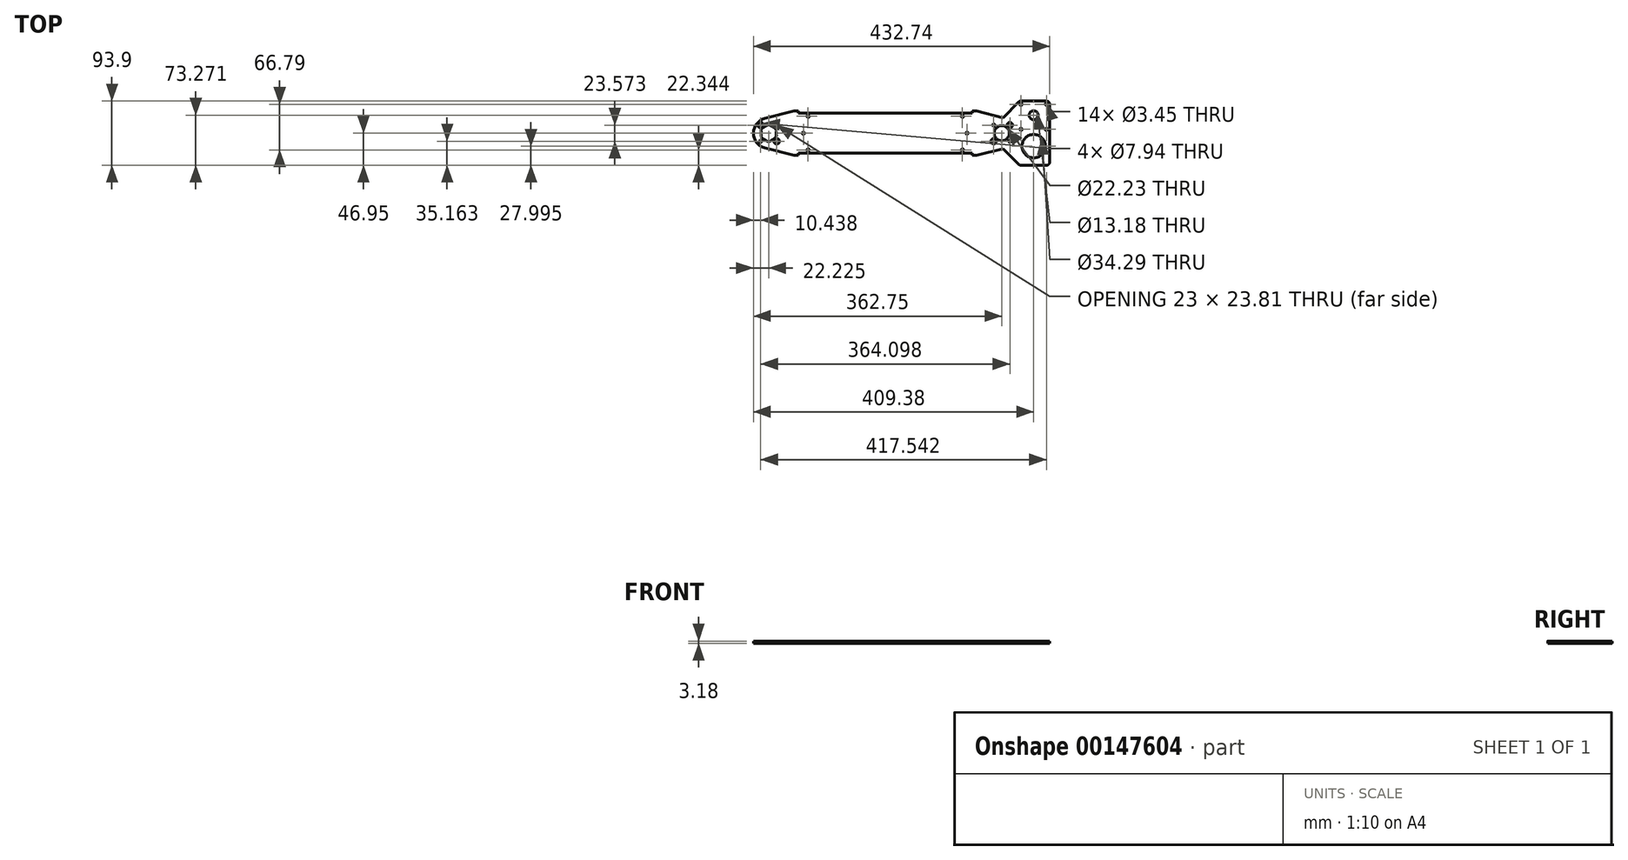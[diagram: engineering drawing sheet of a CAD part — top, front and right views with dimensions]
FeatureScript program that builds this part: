
annotation { "Feature Type Name" : "Feature", "Feature Type Description" : "" }
export const myFeature = defineFeature(function(context is Context, id is Id, definition is map)
    precondition{}
    {
        {
            var Q0;
            Q0=qCreatedBy(makeId("Top.planeOp"),FACE);
            var sketch = newSketch(context, id + "F0", { "sketchPlane" : qUnion([Q0])});
            skPoint(sketch, "E0.rect.middle", {"position": v(0, 0) * mm});
            skCircle(sketch, "E1", {"center": v(0, 0) * mm, "radius": 11.11 * mm});
            skLineSegment(sketch, "E2.bottom", {"start": v(11.79, 11.79) * mm, "end": v(-11.79, 11.79) * mm, "construction": true});
            skLineSegment(sketch, "E2.left", {"start": v(11.79, 11.79) * mm, "end": v(11.79, -11.79) * mm, "construction": true});
            skLineSegment(sketch, "E2.right", {"start": v(-11.79, 11.79) * mm, "end": v(-11.79, -11.79) * mm, "construction": true});
            skCircle(sketch, "E3", {"center": v(-11.79, 11.79) * mm, "radius": 1.73 * mm});
            skCircle(sketch, "E4", {"center": v(11.79, 11.79) * mm, "radius": 3.97 * mm});
            skCircle(sketch, "E5", {"center": v(11.79, -11.79) * mm, "radius": 1.73 * mm});
            skCircle(sketch, "E6", {"center": v(-11.79, -11.79) * mm, "radius": 3.97 * mm});
            skArc(sketch, "E7", {"start": v(-346.1, 21.51) * mm, "mid": v(-362.75, 0) * mm, "end": v(-346.1, -21.51) * mm});
            skLineSegment(sketch, "E8.bottom", {"start": v(-352.31, 11.79) * mm, "end": v(-328.74, 11.79) * mm, "construction": true});
            skLineSegment(sketch, "E8.top", {"start": v(-352.31, -11.79) * mm, "end": v(-328.74, -11.79) * mm, "construction": true});
            skLineSegment(sketch, "E8.left", {"start": v(-352.31, 11.79) * mm, "end": v(-352.31, -11.79) * mm, "construction": true});
            skLineSegment(sketch, "E8.right", {"start": v(-328.74, 11.79) * mm, "end": v(-328.74, -11.79) * mm, "construction": true});
            skCircle(sketch, "E9", {"center": v(-328.74, 11.79) * mm, "radius": 1.73 * mm});
            skCircle(sketch, "E10", {"center": v(-340.53, 0) * mm, "radius": 11.11 * mm});
            skCircle(sketch, "E11", {"center": v(-352.31, 11.79) * mm, "radius": 3.97 * mm});
            skCircle(sketch, "E12", {"center": v(-352.31, -11.79) * mm, "radius": 1.73 * mm});
            skCircle(sketch, "E13", {"center": v(-328.74, -11.79) * mm, "radius": 3.97 * mm});
            skLineSegment(sketch, "E14", {"start": v(0, 0) * mm, "end": v(-340.53, 0) * mm, "construction": true});
            skLineSegment(sketch, "E15", {"start": v(-346.1, -21.51) * mm, "end": v(-303.61, -32.54) * mm});
            skLineSegment(sketch, "E16", {"start": v(-346.1, 21.51) * mm, "end": v(-303.61, 32.54) * mm});
            skLineSegment(sketch, "E17", {"start": v(-297.26, -29.37) * mm, "end": v(-43.26, -29.37) * mm});
            skLineSegment(sketch, "E18", {"start": v(-297.26, 29.37) * mm, "end": v(-43.26, 29.37) * mm});
            skLineSegment(sketch, "E19", {"start": v(-297.26, 32.54) * mm, "end": v(-297.26, 29.37) * mm});
            skLineSegment(sketch, "E20", {"start": v(-297.26, 32.54) * mm, "end": v(-303.61, 32.54) * mm});
            skLineSegment(sketch, "E21", {"start": v(-297.26, -29.37) * mm, "end": v(-297.26, -32.54) * mm});
            skLineSegment(sketch, "E22", {"start": v(-297.26, -32.54) * mm, "end": v(-303.61, -32.54) * mm});
            skLineSegment(sketch, "E23", {"start": v(-43.26, -29.37) * mm, "end": v(-43.26, -32.54) * mm});
            skLineSegment(sketch, "E24", {"start": v(-43.26, -32.54) * mm, "end": v(-36.91, -32.54) * mm});
            skLineSegment(sketch, "E25", {"start": v(-43.26, 29.37) * mm, "end": v(-43.26, 32.54) * mm});
            skLineSegment(sketch, "E26", {"start": v(-43.26, 32.54) * mm, "end": v(-36.91, 32.54) * mm});
            skLineSegment(sketch, "E27", {"start": v(-36.91, -32.54) * mm, "end": v(1.65, -22.53) * mm});
            skLineSegment(sketch, "E28", {"start": v(1.65, 22.53) * mm, "end": v(-36.91, 32.54) * mm});
            skLineSegment(sketch, "E29", {"start": v(-297.26, 29.37) * mm, "end": v(-297.26, 24.6) * mm, "construction": true});
            skLineSegment(sketch, "E30", {"start": v(-297.26, 24.6) * mm, "end": v(-282.98, 24.6) * mm, "construction": true});
            skLineSegment(sketch, "E31", {"start": v(-297.26, -29.37) * mm, "end": v(-297.26, -24.6) * mm, "construction": true});
            skLineSegment(sketch, "E32", {"start": v(-297.26, -24.6) * mm, "end": v(-282.98, -24.6) * mm, "construction": true});
            skLineSegment(sketch, "E33", {"start": v(-43.26, -29.37) * mm, "end": v(-43.26, -24.6) * mm, "construction": true});
            skLineSegment(sketch, "E34", {"start": v(-43.26, -24.6) * mm, "end": v(-57.55, -24.6) * mm, "construction": true});
            skLineSegment(sketch, "E35", {"start": v(-43.26, 29.37) * mm, "end": v(-43.26, 24.6) * mm, "construction": true});
            skLineSegment(sketch, "E36", {"start": v(-43.26, 24.6) * mm, "end": v(-57.55, 24.6) * mm, "construction": true});
            skCircle(sketch, "E37", {"center": v(-282.98, 24.6) * mm, "radius": 1.73 * mm});
            skCircle(sketch, "E38", {"center": v(-57.55, 24.6) * mm, "radius": 1.73 * mm});
            skCircle(sketch, "E39", {"center": v(-57.55, -24.6) * mm, "radius": 1.73 * mm});
            skCircle(sketch, "E40", {"center": v(-282.98, -24.6) * mm, "radius": 1.73 * mm});
            skLineSegment(sketch, "E41", {"start": v(-11.79, -11.79) * mm, "end": v(11.79, -11.79) * mm, "construction": true});
            skLineSegment(sketch, "E42", {"start": v(-170.26, -29.37) * mm, "end": v(-170.26, 0) * mm, "construction": true});
            skLineSegment(sketch, "E43", {"start": v(-170.26, 0) * mm, "end": v(-170.26, 29.37) * mm, "construction": true});
            skLineSegment(sketch, "E44", {"start": v(-328.74, 11.79) * mm, "end": v(-289.73, 11.79) * mm, "construction": true});
            skLineSegment(sketch, "E45", {"start": v(-289.73, 11.79) * mm, "end": v(-289.73, 0) * mm, "construction": true});
            skLineSegment(sketch, "E46", {"start": v(-11.79, 11.79) * mm, "end": v(-50.8, 11.79) * mm, "construction": true});
            skLineSegment(sketch, "E47", {"start": v(-50.8, 11.79) * mm, "end": v(-50.8, 0) * mm, "construction": true});
            skCircle(sketch, "E48", {"center": v(-289.73, 0) * mm, "radius": 1.73 * mm});
            skCircle(sketch, "E49", {"center": v(-50.8, 0) * mm, "radius": 1.73 * mm});
            skLineSegment(sketch, "E50", {"start": v(1.65, 22.53) * mm, "end": v(5.58, 21.51) * mm, "construction": true});
            skLineSegment(sketch, "E51", {"start": v(1.65, -22.53) * mm, "end": v(5.58, -21.51) * mm, "construction": true});
            skLineSegment(sketch, "E52", {"start": v(0, 0) * mm, "end": v(46.63, 0) * mm, "construction": true});
            skLineSegment(sketch, "E53", {"start": v(46.63, 11.59) * mm, "end": v(46.63, -11.59) * mm, "construction": true});
            skLineSegment(sketch, "E54", {"start": v(46.63, 0) * mm, "end": v(70, 0) * mm, "construction": true});
            skLineSegment(sketch, "E55", {"start": v(1.65, 22.53) * mm, "end": v(24.66, 45.55) * mm});
            skLineSegment(sketch, "E56", {"start": v(1.65, -22.53) * mm, "end": v(24.66, -45.55) * mm});
            skArc(sketch, "E57", {"start": v(5.58, -21.51) * mm, "mid": v(22.23, 0) * mm, "end": v(5.58, 21.51) * mm, "construction": true});
            skLineSegment(sketch, "E58", {"start": v(46.63, 11.59) * mm, "end": v(46.63, 26.32) * mm, "construction": true});
            skLineSegment(sketch, "E59", {"start": v(46.63, -11.59) * mm, "end": v(46.63, -26.32) * mm, "construction": true});
            skCircle(sketch, "E60", {"center": v(46.63, 18.95) * mm, "radius": 18.16 * mm, "construction": true});
            skCircle(sketch, "E61", {"center": v(28.03, 42.18) * mm, "radius": 1.73 * mm});
            skCircle(sketch, "E62", {"center": v(65.23, 5.56) * mm, "radius": 1.73 * mm});
            skCircle(sketch, "E63", {"center": v(28.03, 5.56) * mm, "radius": 1.73 * mm});
            skArc(sketch, "E64", {"start": v(28.03, 46.95) * mm, "mid": v(26.2, 46.58) * mm, "end": v(24.66, 45.55) * mm});
            skLineSegment(sketch, "E65", {"start": v(28.03, 46.95) * mm, "end": v(70, 46.95) * mm});
            skLineSegment(sketch, "E66", {"start": v(70, 46.95) * mm, "end": v(70, -46.95) * mm});
            skLineSegment(sketch, "E67", {"start": v(70, -46.95) * mm, "end": v(28.03, -46.95) * mm});
            skArc(sketch, "E68", {"start": v(24.66, -45.55) * mm, "mid": v(26.2, -46.58) * mm, "end": v(28.03, -46.95) * mm});
            skLineSegment(sketch, "E69", {"start": v(46.63, 26.32) * mm, "end": v(46.63, 46.95) * mm, "construction": true});
            skLineSegment(sketch, "E70.bottom", {"start": v(28.03, 42.18) * mm, "end": v(65.23, 42.18) * mm, "construction": true});
            skLineSegment(sketch, "E70.top", {"start": v(28.03, 5.56) * mm, "end": v(65.23, 5.56) * mm, "construction": true});
            skLineSegment(sketch, "E70.left", {"start": v(28.03, 42.18) * mm, "end": v(28.03, 5.56) * mm, "construction": true});
            skLineSegment(sketch, "E70.right", {"start": v(65.23, 42.18) * mm, "end": v(65.23, 5.56) * mm, "construction": true});
            skArc(sketch, "E71", {"start": v(65.23, 0.8) * mm, "mid": v(68.6, 2.19) * mm, "end": v(70, 5.56) * mm, "construction": true});
            skLineSegment(sketch, "E72", {"start": v(65.23, 0.8) * mm, "end": v(46.63, 0.8) * mm, "construction": true});
            skArc(sketch, "E73", {"start": v(70, 5.56) * mm, "mid": v(61.86, 8.92) * mm, "end": v(65.23, 0.8) * mm, "construction": true});
            skPoint(sketch, "E74", {"position": v(46.63, 42.18) * mm});
            skCircle(sketch, "E75", {"center": v(46.63, 26.32) * mm, "radius": 6.59 * mm});
            skCircle(sketch, "E76", {"center": v(65.23, 42.18) * mm, "radius": 1.73 * mm});
            skCircle(sketch, "E77", {"center": v(46.63, -18.95) * mm, "radius": 17.15 * mm});
            skCircle(sketch, "E78", {"center": v(28.03, 5.56) * mm, "radius": 6.35 * mm, "construction": true});
            skSolve(sketch);
        }
        {
            var Q0;
            Q0=qSketchRegion(id+"F0",true);
            extrude(context, id + "F1", {"entities" : qUnion([Q0]), "depth" : 3.17 * mm});
        }
        {
            var Q0;
            Q0=makeQuery(id+"F1.opExtrude","CAP_FACE",FACE,{"disambiguationData":[OSD([sQuery(id+"F0.wireOp",EDGE,"d63eafa0-1946-4b0e-8293-95e246b273c5.rect.bottom"),sQuery(id+"F0.wireOp",EDGE,"d63eafa0-1946-4b0e-8293-95e246b273c5.rect.top"),sQuery(id+"F0.wireOp",EDGE,"5983dcdd-59a7-4b72-80fd-e4567be1ae8a"),sQuery(id+"F0.wireOp",EDGE,"5a538b3e-fc2b-4d64-affd-5d60433388e5"),sQuery(id+"F0.wireOp",EDGE,"72e86de7-b207-474f-aadf-64543fae3f9b"),sQuery(id+"F0.wireOp",EDGE,"1c038800-5bd5-4753-8b38-6da13ef78ef9"),sQuery(id+"F0.wireOp",EDGE,"EbMUZoU6-Ffds-1dNq-SxhE-hPi8oSjhvaod"),sQuery(id+"F0.wireOp",EDGE,"RfgQjzcw-1Izs-lnTa-bWkk-oBHRDQjbZqQC"),sQuery(id+"F0.wireOp",EDGE,"1cCQAcjj-TyQA-3DMx-kDix-v5yZVaaGeXVM"),sQuery(id+"F0.wireOp",EDGE,"7KPu8lni-3ZWA-t6oJ-FRoh-C5MB3aVr7E9B"),sQuery(id+"F0.wireOp",EDGE,"bSzr06ES-7M0i-Fw5H-UJmt-4e4EQGRPIe4n"),sQuery(id+"F0.wireOp",EDGE,"WGsr6OjU-OX8l-mawA-7cCc-MfOuMOY06Cp5"),sQuery(id+"F0.wireOp",EDGE,"9mrz1cDN-18gM-20ra-6VCO-jp25g10tvNn2"),sQuery(id+"F0.wireOp",EDGE,"G0uOisy3-Mq6h-PcKh-Zkf4-CVoCvP3Hii1l"),sQuery(id+"F0.wireOp",EDGE,"1ae556be-0ab9-4322-b48e-98cf5a741ae0"),sQuery(id+"F0.wireOp",EDGE,"676cd913-43f8-42b3-8cdc-a90136d19ef5"),sQuery(id+"F0.wireOp",EDGE,"xnt2EyF8-ZVyQ-RbWD-GIsP-ThkcyX8ZioIH.bottom"),sQuery(id+"F0.wireOp",EDGE,"xnt2EyF8-ZVyQ-RbWD-GIsP-ThkcyX8ZioIH.top"),sQuery(id+"F0.wireOp",EDGE,"xnt2EyF8-ZVyQ-RbWD-GIsP-ThkcyX8ZioIH.left"),sQuery(id+"F0.wireOp",EDGE,"E1"),sQuery(id+"F0.wireOp",EDGE,"Jo9pZc7T-t0kF-vjz1-dNbX-L65bwNqtrrdz"),sQuery(id+"F0.wireOp",EDGE,"lEYoY9t7-PMOS-SVp6-xfnB-Xp9WdWMCDdum"),sQuery(id+"F0.wireOp",EDGE,"s7aM02SC-9XQ7-dueL-DqMg-ZFuJqOofj9mt"),sQuery(id+"F0.wireOp",EDGE,"deKa9ngt-XMq2-GGkr-SZIa-KlyN0U5bcCDe"),sQuery(id+"F0.wireOp",EDGE,"E3"),sQuery(id+"F0.wireOp",EDGE,"E4"),sQuery(id+"F0.wireOp",EDGE,"E5"),sQuery(id+"F0.wireOp",EDGE,"E6"),sQuery(id+"F0.wireOp",EDGE,"E7"),sQuery(id+"F0.wireOp",EDGE,"E9"),sQuery(id+"F0.wireOp",EDGE,"E10"),sQuery(id+"F0.wireOp",EDGE,"E11"),sQuery(id+"F0.wireOp",EDGE,"E12"),sQuery(id+"F0.wireOp",EDGE,"E13")])],"isStart":true});
            var sketch = newSketch(context, id + "F2", { "sketchPlane" : qUnion([Q0])});
            skLineSegment(sketch, "E79", {"start": v(-340.53, 0) * mm, "end": v(-350.15, -5.56) * mm, "construction": true});
            skArc(sketch, "E80", {"start": v(-351.26, -2.88) * mm, "mid": v(-350.15, -5.56) * mm, "end": v(-348.38, -7.86) * mm});
            skLineSegment(sketch, "E81", {"start": v(-340.53, 0) * mm, "end": v(-348.38, -7.86) * mm, "construction": true});
            skLineSegment(sketch, "E82", {"start": v(-340.53, 0) * mm, "end": v(-351.26, -2.88) * mm, "construction": true});
            skLineSegment(sketch, "E83", {"start": v(-348.38, -7.86) * mm, "end": v(-348.94, -8.42) * mm});
            skLineSegment(sketch, "E84", {"start": v(-351.26, -2.88) * mm, "end": v(-352.03, -3.08) * mm});
            skArc(sketch, "E85", {"start": v(-352.03, -3.08) * mm, "mid": v(-350.84, -5.95) * mm, "end": v(-348.94, -8.42) * mm});
            skLineSegment(sketch, "E86", {"start": v(-340.53, 0) * mm, "end": v(-351.64, 0) * mm, "construction": true});
            skSolve(sketch);
        }
        {
            var Q0;
            Q0=qSketchRegion(id+"F2",true);
            var Q1;
            Q1=makeQuery(id+"F1.opExtrude","CAP_FACE",FACE,{"disambiguationData":[OSD([sQuery(id+"F0.wireOp",EDGE,"d63eafa0-1946-4b0e-8293-95e246b273c5.rect.bottom"),sQuery(id+"F0.wireOp",EDGE,"d63eafa0-1946-4b0e-8293-95e246b273c5.rect.top"),sQuery(id+"F0.wireOp",EDGE,"5983dcdd-59a7-4b72-80fd-e4567be1ae8a"),sQuery(id+"F0.wireOp",EDGE,"5a538b3e-fc2b-4d64-affd-5d60433388e5"),sQuery(id+"F0.wireOp",EDGE,"72e86de7-b207-474f-aadf-64543fae3f9b"),sQuery(id+"F0.wireOp",EDGE,"1c038800-5bd5-4753-8b38-6da13ef78ef9"),sQuery(id+"F0.wireOp",EDGE,"EbMUZoU6-Ffds-1dNq-SxhE-hPi8oSjhvaod"),sQuery(id+"F0.wireOp",EDGE,"RfgQjzcw-1Izs-lnTa-bWkk-oBHRDQjbZqQC"),sQuery(id+"F0.wireOp",EDGE,"1cCQAcjj-TyQA-3DMx-kDix-v5yZVaaGeXVM"),sQuery(id+"F0.wireOp",EDGE,"7KPu8lni-3ZWA-t6oJ-FRoh-C5MB3aVr7E9B"),sQuery(id+"F0.wireOp",EDGE,"bSzr06ES-7M0i-Fw5H-UJmt-4e4EQGRPIe4n"),sQuery(id+"F0.wireOp",EDGE,"WGsr6OjU-OX8l-mawA-7cCc-MfOuMOY06Cp5"),sQuery(id+"F0.wireOp",EDGE,"9mrz1cDN-18gM-20ra-6VCO-jp25g10tvNn2"),sQuery(id+"F0.wireOp",EDGE,"G0uOisy3-Mq6h-PcKh-Zkf4-CVoCvP3Hii1l"),sQuery(id+"F0.wireOp",EDGE,"1ae556be-0ab9-4322-b48e-98cf5a741ae0"),sQuery(id+"F0.wireOp",EDGE,"676cd913-43f8-42b3-8cdc-a90136d19ef5"),sQuery(id+"F0.wireOp",EDGE,"xnt2EyF8-ZVyQ-RbWD-GIsP-ThkcyX8ZioIH.bottom"),sQuery(id+"F0.wireOp",EDGE,"xnt2EyF8-ZVyQ-RbWD-GIsP-ThkcyX8ZioIH.top"),sQuery(id+"F0.wireOp",EDGE,"xnt2EyF8-ZVyQ-RbWD-GIsP-ThkcyX8ZioIH.left"),sQuery(id+"F0.wireOp",EDGE,"E1"),sQuery(id+"F0.wireOp",EDGE,"Jo9pZc7T-t0kF-vjz1-dNbX-L65bwNqtrrdz"),sQuery(id+"F0.wireOp",EDGE,"lEYoY9t7-PMOS-SVp6-xfnB-Xp9WdWMCDdum"),sQuery(id+"F0.wireOp",EDGE,"s7aM02SC-9XQ7-dueL-DqMg-ZFuJqOofj9mt"),sQuery(id+"F0.wireOp",EDGE,"deKa9ngt-XMq2-GGkr-SZIa-KlyN0U5bcCDe"),sQuery(id+"F0.wireOp",EDGE,"E3"),sQuery(id+"F0.wireOp",EDGE,"E4"),sQuery(id+"F0.wireOp",EDGE,"E5"),sQuery(id+"F0.wireOp",EDGE,"E6"),sQuery(id+"F0.wireOp",EDGE,"E7"),sQuery(id+"F0.wireOp",EDGE,"E9"),sQuery(id+"F0.wireOp",EDGE,"E10"),sQuery(id+"F0.wireOp",EDGE,"E11"),sQuery(id+"F0.wireOp",EDGE,"E12"),sQuery(id+"F0.wireOp",EDGE,"E13")])],"isStart":false});
            extrude(context, id + "F3", {"entities" : qUnion([Q0]), "operationType" : NewBodyOperationType.REMOVE, "endBound" : BoundingType.UP_TO_SURFACE, "oppositeDirection" : true, "endBoundEntityFace" : qUnion([Q1]), "depth" : 25.4 * mm});
        }
        {
            var Q0;
            Q0=makeQuery(id+"F3.boolean.opBoolean","COPY",FACE,{"derivedFrom":makeQuery(id+"F3.opExtrude","SWEPT_FACE",FACE,{"disambiguationData":[OSD([sQuery(id+"F2.wireOp",EDGE,"E83")])]})});
            var Q1;
            Q1=makeQuery(id+"F3.boolean.opBoolean","COPY",FACE,{"derivedFrom":makeQuery(id+"F3.opExtrude","SWEPT_FACE",FACE,{"disambiguationData":[OSD([sQuery(id+"F2.wireOp",EDGE,"E85")])]})});
            var Q2;
            Q2=makeQuery(id+"F3.boolean.opBoolean","COPY",FACE,{"derivedFrom":makeQuery(id+"F3.opExtrude","SWEPT_FACE",FACE,{"disambiguationData":[OSD([sQuery(id+"F2.wireOp",EDGE,"E84")])]})});
            var Q3;
            Q3=makeQuery(id+"F1.opExtrude","SWEPT_FACE",FACE,{"disambiguationData":[OSD([sQuery(id+"F0.wireOp",EDGE,"E10")])]});
            circularPattern(context, id + "F4", {"patternType" : PatternType.FACE, "faces" : qUnion([Q0, Q1, Q2]), "axis" : qUnion([Q3]), "angle" : 60 * degree, "instanceCount" : 6});
        }
        {
            var Q0;
            Q0=makeQuery(id+"F1.opExtrude","SWEPT_EDGE",EDGE,{"disambiguationData":[OSD([sQuery(id+"F0.wireOp",EDGE,"E65"),sQuery(id+"F0.wireOp",EDGE,"E66")])]});
            var Q1;
            Q1=makeQuery(id+"F1.opExtrude","SWEPT_EDGE",EDGE,{"disambiguationData":[OSD([sQuery(id+"F0.wireOp",EDGE,"E66"),sQuery(id+"F0.wireOp",EDGE,"E67")])]});
            fillet(context, id + "F5", {"entities" : qUnion([Q0, Q1]), "radius" : 4.76 * mm, "tangentPropagation" : true, "allowEdgeOverflow" : false});
        }
    });
